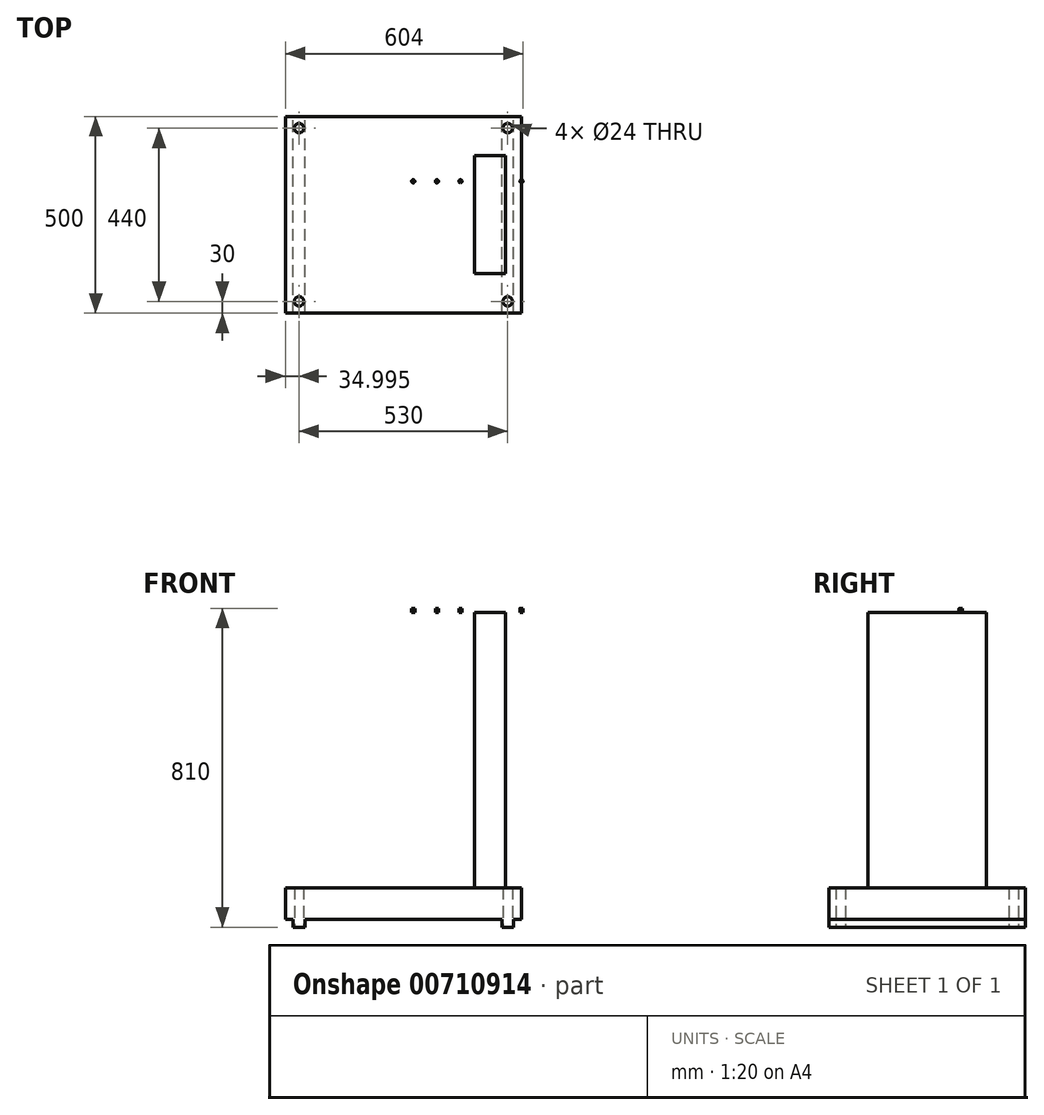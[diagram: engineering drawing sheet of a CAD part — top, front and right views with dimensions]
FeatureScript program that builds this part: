
annotation { "Feature Type Name" : "Feature", "Feature Type Description" : "" }
export const myFeature = defineFeature(function(context is Context, id is Id, definition is map)
    precondition{}
    {
        {
            var Q0;
            Q0=qCreatedBy(makeId("Front.planeOp"),FACE);
            var sketch = newSketch(context, id + "F0", { "sketchPlane" : qUnion([Q0])});
            skLineSegment(sketch, "E0", {"start": v(-263.24, 80) * mm, "end": v(336.76, 80) * mm});
            skLineSegment(sketch, "E1", {"start": v(336.76, 80) * mm, "end": v(336.76, 0) * mm});
            skLineSegment(sketch, "E2", {"start": v(336.76, 0) * mm, "end": v(316.76, 0) * mm});
            skLineSegment(sketch, "E3", {"start": v(316.76, 0) * mm, "end": v(316.76, -20) * mm});
            skLineSegment(sketch, "E4", {"start": v(316.76, -20) * mm, "end": v(286.76, -20) * mm});
            skLineSegment(sketch, "E5", {"start": v(286.76, -20) * mm, "end": v(286.76, 0) * mm});
            skLineSegment(sketch, "E6", {"start": v(286.76, 0) * mm, "end": v(-213.24, 0) * mm});
            skLineSegment(sketch, "E7", {"start": v(-213.24, 0) * mm, "end": v(-213.24, -20) * mm});
            skLineSegment(sketch, "E8", {"start": v(-213.24, -20) * mm, "end": v(-243.24, -20) * mm});
            skLineSegment(sketch, "E9", {"start": v(-243.24, -20) * mm, "end": v(-243.24, 0) * mm});
            skLineSegment(sketch, "E10", {"start": v(-243.24, 0) * mm, "end": v(-263.24, 0) * mm});
            skLineSegment(sketch, "E11", {"start": v(-263.24, 0) * mm, "end": v(-263.24, 80) * mm});
            skSolve(sketch);
        }
        {
            var Q0;
            Q0=makeQuery(id+"F0.imprint","IMPRINT",FACE,{"disambiguationData":[TD([[makeQuery(id+"F0.imprint","IMPRINT",EDGE,{"derivedFrom":sQuery(id+"F0.wireOp",EDGE,"E0")}),-1.0]])]});
            extrude(context, id + "F1", {"entities" : qUnion([Q0]), "depth" : 500 * mm, "offsetDistance" : 25 * mm});
        }
        {
            var Q0;
            Q0=makeQuery(id+"F1.opExtrude","SWEPT_FACE",FACE,{"disambiguationData":[OSD([sQuery(id+"F0.wireOp",EDGE,"E0")])]});
            var sketch = newSketch(context, id + "F2", { "sketchPlane" : qUnion([Q0])});
            skLineSegment(sketch, "E12", {"start": v(336.76, -250) * mm, "end": v(-263.24, -250) * mm, "construction": true});
            skLineSegment(sketch, "E13", {"start": v(256.76, -500) * mm, "end": v(256.76, 0) * mm, "construction": true});
            skLineSegment(sketch, "E14.bottom", {"start": v(296.76, -100) * mm, "end": v(216.76, -100) * mm});
            skLineSegment(sketch, "E14.top", {"start": v(296.76, -400) * mm, "end": v(216.76, -400) * mm});
            skLineSegment(sketch, "E14.left", {"start": v(296.76, -100) * mm, "end": v(296.76, -400) * mm});
            skLineSegment(sketch, "E14.right", {"start": v(216.76, -100) * mm, "end": v(216.76, -400) * mm});
            skPoint(sketch, "E14.middle", {"position": v(256.76, -250) * mm});
            skSolve(sketch);
        }
        {
            var Q0;
            Q0=makeQuery(id+"F1.opExtrude","SWEPT_FACE",FACE,{"disambiguationData":[OSD([sQuery(id+"F0.wireOp",EDGE,"E8")])]});
            var sketch = newSketch(context, id + "F3", { "sketchPlane" : qUnion([Q0])});
            skLineSegment(sketch, "E15", {"start": v(-228.24, 500) * mm, "end": v(-228.24, 0) * mm, "construction": true});
            skCircle(sketch, "E16", {"center": v(-228.24, 470) * mm, "radius": 12 * mm});
            skCircle(sketch, "E17", {"center": v(-228.24, 30) * mm, "radius": 12 * mm});
            skSolve(sketch);
        }
        {
            var Q0;
            Q0=makeQuery(id+"F1.opExtrude","SWEPT_FACE",FACE,{"disambiguationData":[OSD([sQuery(id+"F0.wireOp",EDGE,"E4")])]});
            var sketch = newSketch(context, id + "F4", { "sketchPlane" : qUnion([Q0])});
            skLineSegment(sketch, "E18", {"start": v(301.76, 500) * mm, "end": v(301.76, 0) * mm, "construction": true});
            skCircle(sketch, "E19", {"center": v(301.76, 470) * mm, "radius": 12 * mm});
            skCircle(sketch, "E20", {"center": v(301.76, 30) * mm, "radius": 12 * mm});
            skSolve(sketch);
        }
        {
            var Q0;
            Q0=makeQuery(id+"F4.imprint","IMPRINT",FACE,{"disambiguationData":[TD([[makeQuery(id+"F4.imprint","IMPRINT",EDGE,{"derivedFrom":sQuery(id+"F4.wireOp",EDGE,"E19")}),1.0]])]});
            var Q1;
            Q1=makeQuery(id+"F4.imprint","IMPRINT",FACE,{"disambiguationData":[TD([[makeQuery(id+"F4.imprint","IMPRINT",EDGE,{"derivedFrom":sQuery(id+"F4.wireOp",EDGE,"E20")}),1.0]])]});
            var Q2;
            Q2=makeQuery(id+"F3.imprint","IMPRINT",FACE,{"disambiguationData":[TD([[makeQuery(id+"F3.imprint","IMPRINT",EDGE,{"derivedFrom":sQuery(id+"F3.wireOp",EDGE,"E17")}),1.0]])]});
            var Q3;
            Q3=makeQuery(id+"F3.imprint","IMPRINT",FACE,{"disambiguationData":[TD([[makeQuery(id+"F3.imprint","IMPRINT",EDGE,{"derivedFrom":sQuery(id+"F3.wireOp",EDGE,"E16")}),1.0]])]});
            extrude(context, id + "F5", {"entities" : qUnion([Q0, Q1, Q2, Q3]), "operationType" : NewBodyOperationType.REMOVE, "endBound" : BoundingType.THROUGH_ALL, "oppositeDirection" : true, "depth" : 100 * mm, "offsetDistance" : 25 * mm});
        }
        {
            var Q0;
            Q0=makeQuery(id+"F2.imprint","IMPRINT",FACE,{"disambiguationData":[TD([[makeQuery(id+"F2.imprint","IMPRINT",EDGE,{"derivedFrom":sQuery(id+"F2.wireOp",EDGE,"E14.bottom")}),1.0]])]});
            extrude(context, id + "F6", {"entities" : qUnion([Q0]), "depth" : 700 * mm, "offsetDistance" : 25 * mm});
        }
        {
            var Q0;
            Q0=makeQuery(id+"F6.opExtrude","CAP_FACE",FACE,{"disambiguationData":[OSD([sQuery(id+"F2.wireOp",EDGE,"E14.bottom"),sQuery(id+"F2.wireOp",EDGE,"E14.top"),sQuery(id+"F2.wireOp",EDGE,"E14.left"),sQuery(id+"F2.wireOp",EDGE,"E14.right")])],"isStart":false});
            var sketch = newSketch(context, id + "F7", { "sketchPlane" : qUnion([Q0])});
            skLineSegment(sketch, "E21.bottom", {"start": v(366.76, -100) * mm, "end": v(41.76, -100) * mm});
            skLineSegment(sketch, "E21.top", {"start": v(366.76, -400) * mm, "end": v(41.76, -400) * mm});
            skLineSegment(sketch, "E21.left", {"start": v(366.76, -100) * mm, "end": v(366.76, -400) * mm});
            skLineSegment(sketch, "E21.right", {"start": v(41.76, -100) * mm, "end": v(41.76, -400) * mm});
            skSolve(sketch);
        }
        {
            var Q0;
            {var subQ1=makeQuery(id+"F6.opExtrude","CAP_EDGE",EDGE,{"disambiguationData":[OSD([sQuery(id+"F2.wireOp",EDGE,"E14.left")])],"isStart":false});Q0=makeQuery(id+"F7.imprint","IMPRINT",FACE,{"disambiguationData":[TD([[makeQuery(id+"F7.imprint","IMPRINT",EDGE,{"derivedFrom":subQ1}),-1.0]])]});}
            var Q1;
            {var subQ2=sQuery(id+"F7.wireOp",EDGE,"E21.right");Q1=makeQuery(id+"F7.imprint","IMPRINT",FACE,{"disambiguationData":[TD([[makeQuery(id+"F7.imprint","IMPRINT",EDGE,{"derivedFrom":subQ2}),1.0]])]});}
            var Q2;
            {var subQ2=sQuery(id+"F7.wireOp",EDGE,"E21.left");Q2=makeQuery(id+"F7.imprint","IMPRINT",FACE,{"disambiguationData":[TD([[makeQuery(id+"F7.imprint","IMPRINT",EDGE,{"derivedFrom":subQ2}),-1.0]])]});}
            extrude(context, id + "F8", {"entities" : qUnion([Q0, Q1, Q2]), "depth" : 10 * mm, "offsetDistance" : 25 * mm});
        }
        {
            var Q0;
            Q0=makeQuery(id+"F8.opExtrude","CAP_FACE",FACE,{"disambiguationData":[OSD([sQuery(id+"F7.wireOp",EDGE,"E21.bottom"),sQuery(id+"F7.wireOp",EDGE,"E21.top"),sQuery(id+"F7.wireOp",EDGE,"E21.left"),sQuery(id+"F7.wireOp",EDGE,"E21.right")])],"isStart":false});
            var sketch = newSketch(context, id + "F9", { "sketchPlane" : qUnion([Q0])});
            skLineSegment(sketch, "E22", {"start": v(41.76, -250) * mm, "end": v(366.76, -250) * mm, "construction": true});
            skCircle(sketch, "E23", {"center": v(336.76, -335) * mm, "radius": 4 * mm});
            skCircle(sketch, "E24.MirrorC", {"center": v(336.76, -165) * mm, "radius": 4 * mm});
            skLineSegment(sketch, "E25", {"start": v(61.76, -400) * mm, "end": v(61.76, -100) * mm, "construction": true});
            skCircle(sketch, "E26", {"center": v(61.76, -335) * mm, "radius": 4 * mm});
            skCircle(sketch, "E27", {"center": v(121.76, -335) * mm, "radius": 4 * mm});
            skCircle(sketch, "E28", {"center": v(181.76, -335) * mm, "radius": 4 * mm});
            skCircle(sketch, "E29.MirrorC", {"center": v(61.76, -165) * mm, "radius": 4 * mm});
            skCircle(sketch, "E30.MirrorC", {"center": v(121.76, -165) * mm, "radius": 4 * mm});
            skCircle(sketch, "E31.MirrorC", {"center": v(181.76, -165) * mm, "radius": 4 * mm});
            skSolve(sketch);
        }
        {
            var Q0;
            Q0=makeQuery(id+"F9.imprint","IMPRINT",FACE,{"disambiguationData":[TD([[makeQuery(id+"F9.imprint","IMPRINT",EDGE,{"derivedFrom":sQuery(id+"F9.wireOp",EDGE,"E27")}),1.0]])]});
            var Q1;
            Q1=makeQuery(id+"F9.imprint","IMPRINT",FACE,{"disambiguationData":[TD([[makeQuery(id+"F9.imprint","IMPRINT",EDGE,{"derivedFrom":sQuery(id+"F9.wireOp",EDGE,"E26")}),1.0]])]});
            var Q2;
            Q2=makeQuery(id+"F9.imprint","IMPRINT",FACE,{"disambiguationData":[TD([[makeQuery(id+"F9.imprint","IMPRINT",EDGE,{"derivedFrom":sQuery(id+"F9.wireOp",EDGE,"E28")}),1.0]])]});
            var Q3;
            Q3=makeQuery(id+"F9.imprint","IMPRINT",FACE,{"disambiguationData":[TD([[makeQuery(id+"F9.imprint","IMPRINT",EDGE,{"derivedFrom":sQuery(id+"F9.wireOp",EDGE,"E23")}),1.0]])]});
            var Q4;
            Q4=makeQuery(id+"F9.imprint","IMPRINT",FACE,{"disambiguationData":[TD([[makeQuery(id+"F9.imprint","IMPRINT",EDGE,{"derivedFrom":sQuery(id+"F9.wireOp",EDGE,"E24.MirrorC")}),-1.0]])]});
            var Q5;
            Q5=makeQuery(id+"F9.imprint","IMPRINT",FACE,{"disambiguationData":[TD([[makeQuery(id+"F9.imprint","IMPRINT",EDGE,{"derivedFrom":sQuery(id+"F9.wireOp",EDGE,"E31.MirrorC")}),-1.0]])]});
            var Q6;
            Q6=makeQuery(id+"F9.imprint","IMPRINT",FACE,{"disambiguationData":[TD([[makeQuery(id+"F9.imprint","IMPRINT",EDGE,{"derivedFrom":sQuery(id+"F9.wireOp",EDGE,"E30.MirrorC")}),-1.0]])]});
            var Q7;
            Q7=makeQuery(id+"F9.imprint","IMPRINT",FACE,{"disambiguationData":[TD([[makeQuery(id+"F9.imprint","IMPRINT",EDGE,{"derivedFrom":sQuery(id+"F9.wireOp",EDGE,"E29.MirrorC")}),-1.0]])]});
            extrude(context, id + "F10", {"entities" : qUnion([Q0, Q1, Q2, Q3, Q4, Q5, Q6, Q7]), "operationType" : NewBodyOperationType.REMOVE, "oppositeDirection" : true, "depth" : 10 * mm, "offsetDistance" : 25 * mm});
        }
    });
